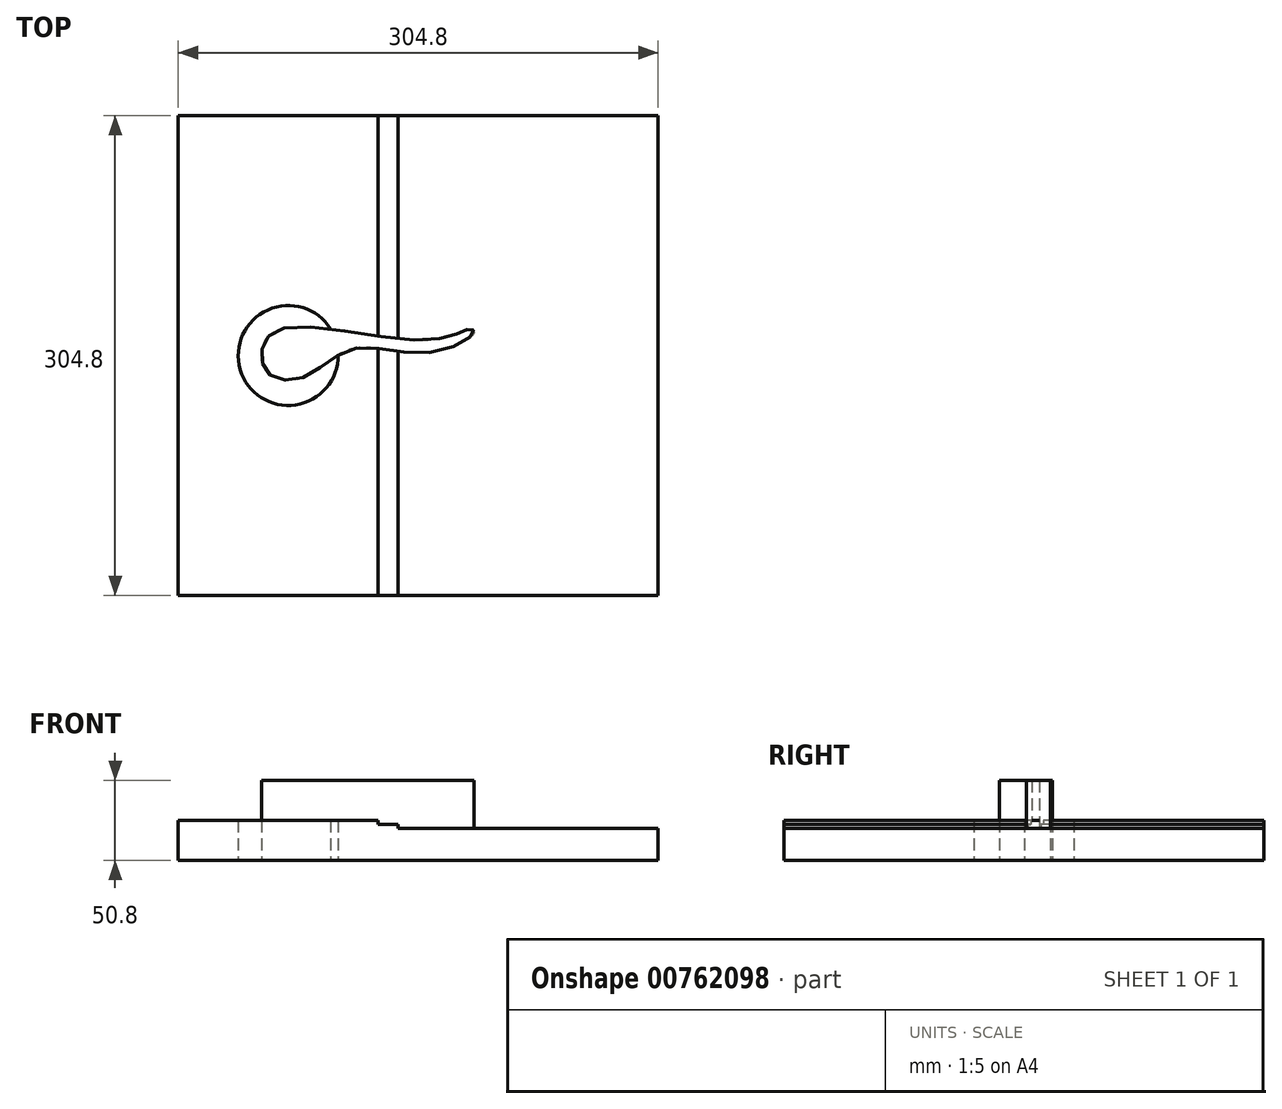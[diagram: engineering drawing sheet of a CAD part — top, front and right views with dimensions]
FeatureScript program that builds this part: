
annotation { "Feature Type Name" : "Feature", "Feature Type Description" : "" }
export const myFeature = defineFeature(function(context is Context, id is Id, definition is map)
    precondition{}
    {
        {
            var Q0;
            Q0=qCreatedBy(makeId("Top.planeOp"),FACE);
            var sketch = newSketch(context, id + "F0", { "sketchPlane" : qUnion([Q0])});
            skLineSegment(sketch, "E0.bottom", {"start": v(0, 0) * mm, "end": v(304.8, 0) * mm});
            skLineSegment(sketch, "E0.top", {"start": v(0, 304.8) * mm, "end": v(304.8, 304.8) * mm});
            skLineSegment(sketch, "E0.left", {"start": v(0, 0) * mm, "end": v(0, 304.8) * mm});
            skLineSegment(sketch, "E0.right", {"start": v(304.8, 0) * mm, "end": v(304.8, 304.8) * mm});
            skLineSegment(sketch, "E1", {"start": v(127, 304.8) * mm, "end": v(127, 0) * mm});
            skLineSegment(sketch, "E2", {"start": v(139.7, 304.8) * mm, "end": v(139.7, 0) * mm});
            skCircle(sketch, "E3", {"center": v(69.85, 152.4) * mm, "radius": 31.75 * mm});
            skLineSegment(sketch, "E4", {"start": v(69.85, 304.8) * mm, "end": v(69.85, 0) * mm, "construction": true});
            skSolve(sketch);
        }
        {
            var Q0;
            {var subQ0=sQuery(id+"F0.wireOp",EDGE,"E0.left");Q0=makeQuery(id+"F0.imprint","IMPRINT",FACE,{"disambiguationData":[TD([[makeQuery(id+"F0.imprint","IMPRINT",EDGE,{"derivedFrom":subQ0}),-1.0]])]});}
            extrude(context, id + "F1", {"entities" : qUnion([Q0]), "depth" : 25.4 * mm, "offsetDistance" : 25.4 * mm});
        }
        {
            var Q0;
            {var subQ0=sQuery(id+"F0.wireOp",EDGE,"E1");Q0=makeQuery(id+"F0.imprint","IMPRINT",FACE,{"disambiguationData":[TD([[makeQuery(id+"F0.imprint","IMPRINT",EDGE,{"derivedFrom":subQ0}),1.0]])]});}
            extrude(context, id + "F2", {"entities" : qUnion([Q0]), "operationType" : NewBodyOperationType.ADD, "depth" : 22.86 * mm, "offsetDistance" : 25.4 * mm});
        }
        {
            var Q0;
            {var subQ0=sQuery(id+"F0.wireOp",EDGE,"E0.right");Q0=makeQuery(id+"F0.imprint","IMPRINT",FACE,{"disambiguationData":[TD([[makeQuery(id+"F0.imprint","IMPRINT",EDGE,{"derivedFrom":subQ0}),1.0]])]});}
            extrude(context, id + "F3", {"entities" : qUnion([Q0]), "operationType" : NewBodyOperationType.ADD, "depth" : 20.32 * mm, "offsetDistance" : 25.4 * mm});
        }
        {
            var Q0;
            Q0=qCreatedBy(makeId("Top.planeOp"),FACE);
            var sketch = newSketch(context, id + "F4", { "sketchPlane" : qUnion([Q0])});
            skFitSpline(sketch, "E5", {"points": [v(53.3, 156.55) * mm, v(67.76, 169.8) * mm, v(156.9, 162.17) * mm, v(181.8, 168.2) * mm, v(186.6, 169) * mm, v(187.81, 167) * mm, v(159.7, 154.14) * mm, v(110.32, 156.55) * mm, v(79.8, 138.48) * mm, v(57.32, 140.9) * mm, v(53.3, 156.55) * mm]});
            skSolve(sketch);
        }
        {
            var Q0;
            Q0 = qSketchRegion(id + "F4", true);
            extrude(context, id + "F5", {"entities" : qUnion([Q0]), "operationType" : NewBodyOperationType.ADD, "depth" : 50.8 * mm, "offsetDistance" : 25.4 * mm});
        }
    });
